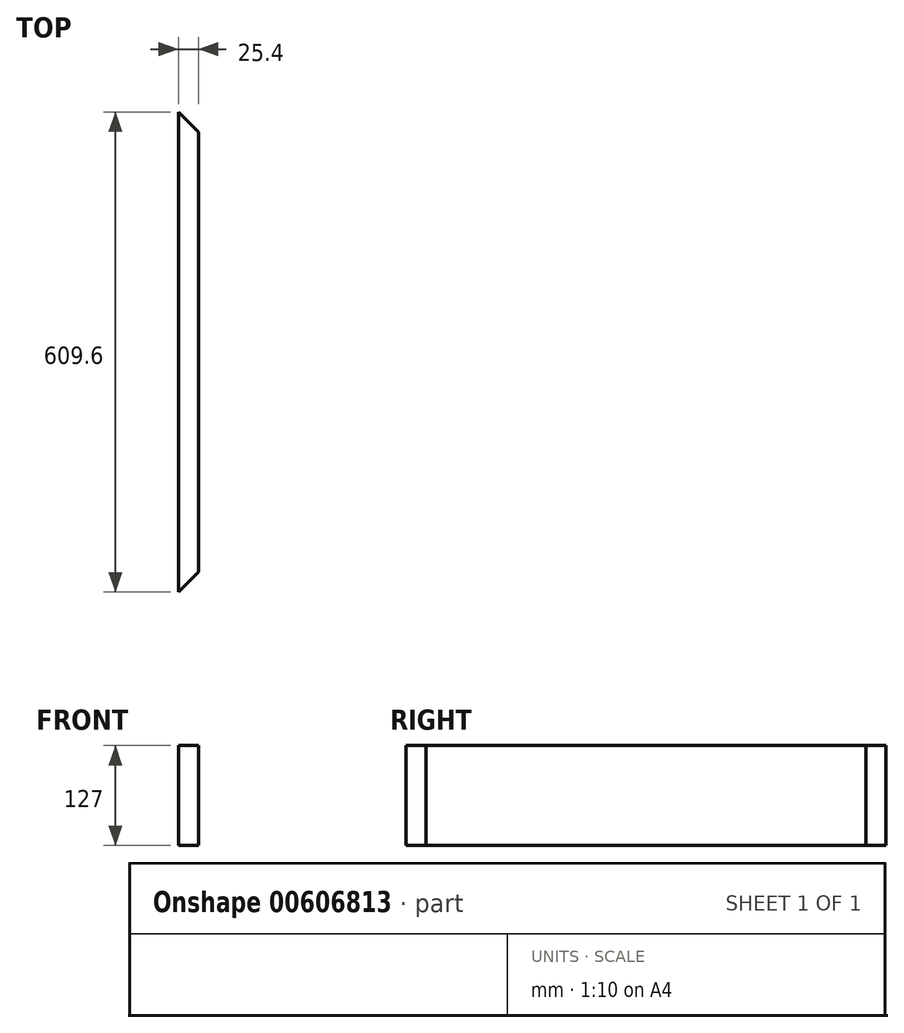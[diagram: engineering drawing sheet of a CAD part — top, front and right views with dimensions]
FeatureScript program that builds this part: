
annotation { "Feature Type Name" : "Feature", "Feature Type Description" : "" }
export const myFeature = defineFeature(function(context is Context, id is Id, definition is map)
    precondition{}
    {
        {
            var Q0;
            Q0=qCreatedBy(makeId("Top.planeOp"),FACE);
            var sketch = newSketch(context, id + "F0", { "sketchPlane" : qUnion([Q0])});
            skLineSegment(sketch, "E0", {"start": v(0, 0) * mm, "end": v(0, 609.6) * mm});
            skPoint(sketch, "E1.endSnap0", {"position": v(0, 304.8) * mm});
            skLineSegment(sketch, "E2", {"start": v(25.4, 302.26) * mm, "end": v(25.4, 584.2) * mm});
            skLineSegment(sketch, "E3", {"start": v(25.4, 302.26) * mm, "end": v(25.4, 25.4) * mm});
            skLineSegment(sketch, "E4", {"start": v(0, 609.6) * mm, "end": v(25.4, 584.2) * mm});
            skLineSegment(sketch, "E5", {"start": v(25.4, 25.4) * mm, "end": v(0, 0) * mm});
            skSolve(sketch);
        }
        {
            var Q0;
            Q0=qSketchRegion(id+"F0",true);
            extrude(context, id + "F1", {"entities" : qUnion([Q0]), "depth" : 127 * mm, "offsetDistance" : 25.4 * mm});
        }
    });
